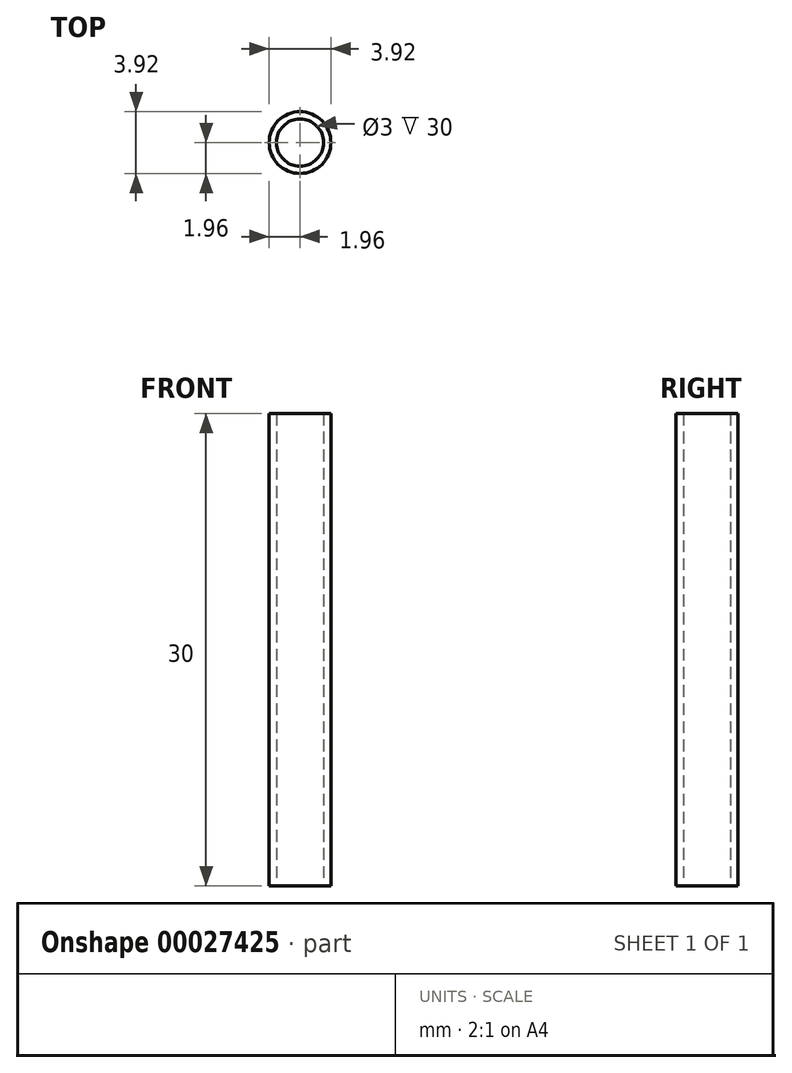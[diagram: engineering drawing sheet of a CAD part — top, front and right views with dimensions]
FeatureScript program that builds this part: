
annotation { "Feature Type Name" : "Feature", "Feature Type Description" : "" }
export const myFeature = defineFeature(function(context is Context, id is Id, definition is map)
    precondition{}
    {
        {
            var Q0;
            Q0=qCreatedBy(makeId("Top.planeOp"),FACE);
            var sketch = newSketch(context, id + "F0", { "sketchPlane" : qUnion([Q0])});
            skCircle(sketch, "E0", {"center": v(0, 0) * mm, "radius": 1.5 * mm});
            skCircle(sketch, "E1", {"center": v(0, 0) * mm, "radius": 1.96 * mm});
            skSolve(sketch);
        }
        {
            var Q0;
            Q0=makeQuery(id+"F0.imprint","IMPRINT",FACE,{"disambiguationData":[TD([[makeQuery(id+"F0.imprint","IMPRINT",EDGE,{"derivedFrom":sQuery(id+"F0.wireOp",EDGE,"E0")}),-1.0]])]});
            extrude(context, id + "F1", {"entities" : qUnion([Q0]), "depth" : 30 * mm});
        }
    });
